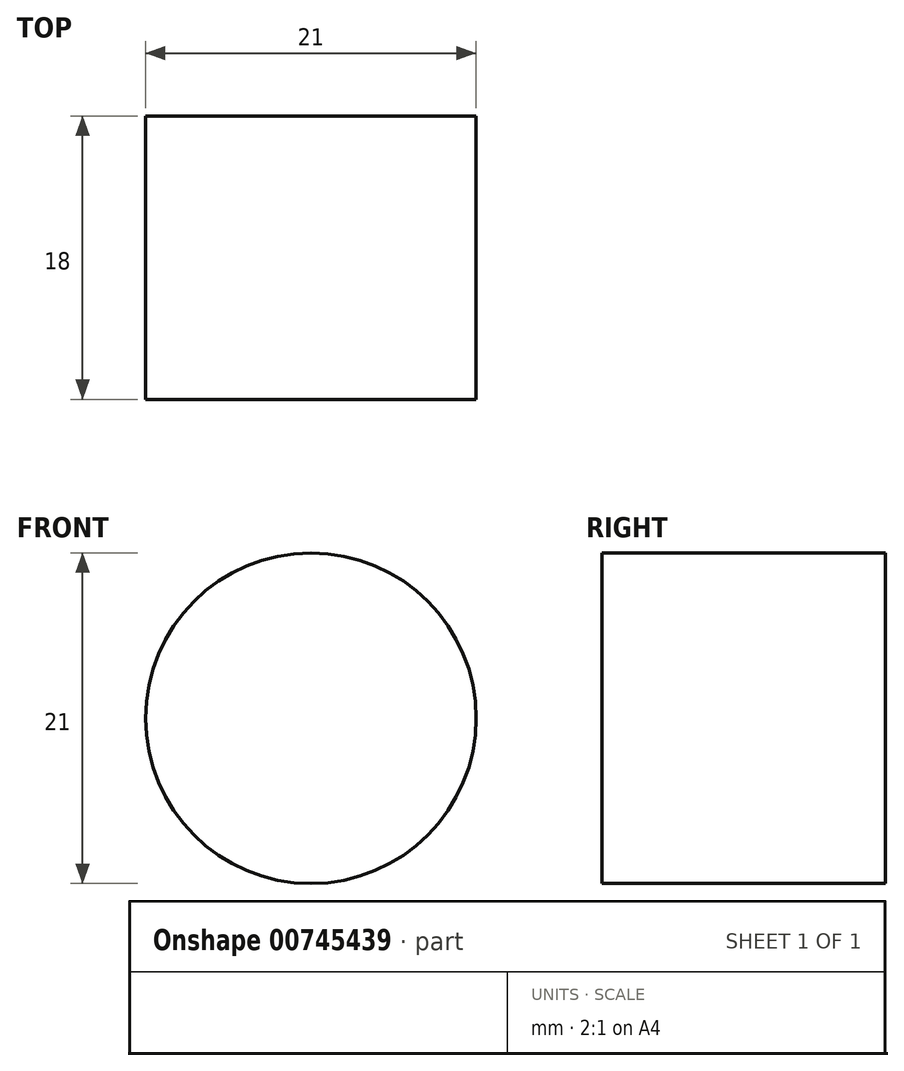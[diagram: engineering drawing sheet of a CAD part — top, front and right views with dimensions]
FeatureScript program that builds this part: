
annotation { "Feature Type Name" : "Feature", "Feature Type Description" : "" }
export const myFeature = defineFeature(function(context is Context, id is Id, definition is map)
    precondition{}
    {
        {
            var Q0;
            Q0=qCreatedBy(makeId("Front.planeOp"),FACE);
            var sketch = newSketch(context, id + "F0", { "sketchPlane" : qUnion([Q0])});
            skCircle(sketch, "E0", {"center": v(0, 0) * mm, "radius": 10.5 * mm});
            skSolve(sketch);
        }
        {
            var Q0;
            Q0 = qSketchRegion(id + "F0", true);
            extrude(context, id + "F1", {"entities" : qUnion([Q0]), "depth" : 18 * mm, "offsetDistance" : 25 * mm});
        }
    });
